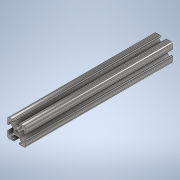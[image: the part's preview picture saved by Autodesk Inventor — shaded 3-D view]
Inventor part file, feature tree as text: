
AUTODESK INVENTOR PART (.ipt)
format: ipt  version: 2020 (Build 240168000, 168)  size: 238,592 bytes
history: native  units: in
note: dims shown in document units (in); Inventor stores cm internally (conversion verified against a paired STEP export)
features: extrude x1, sketch x1
ambient origin geometry x8: Origin, YZ Plane, XZ Plane, XY Plane, X Axis, Y Axis, Z Axis, Center Point
bodies: Solid1 (feature_tree)
feature tree (2):
  extrude  "Extrusion1"  [1 undecoded]
  sketch  "Sketch1"  dims[d0=8.0in d1=0.0in]
note: 1 required parameter value undecoded (feature->parameter linkage not recoverable at this tier; creation-order binding heuristic only, values carry confidence <= 0.55)
